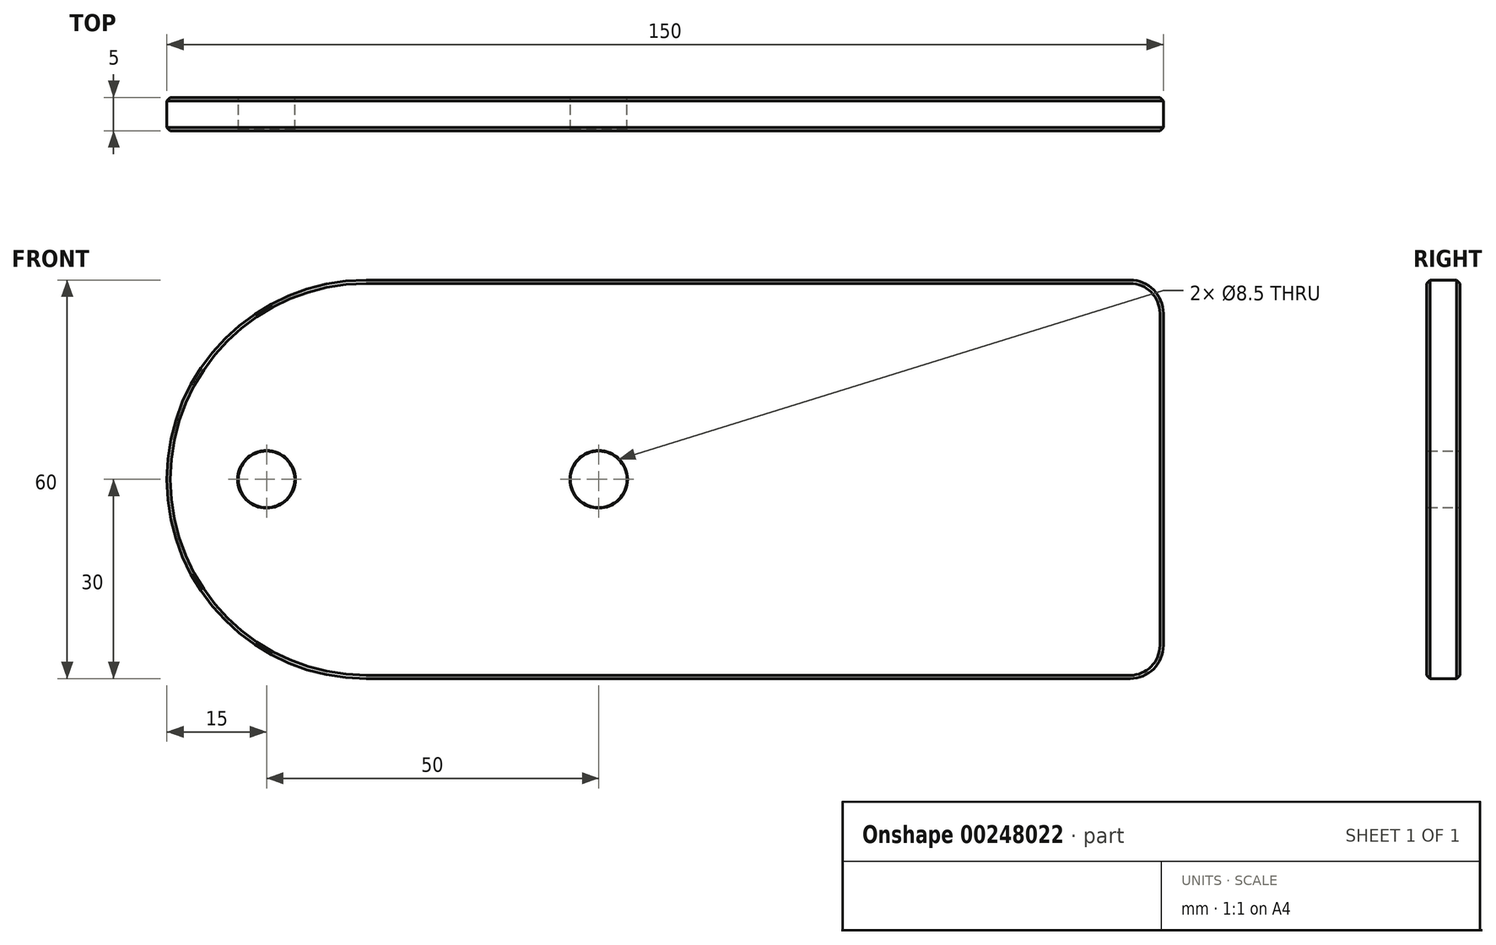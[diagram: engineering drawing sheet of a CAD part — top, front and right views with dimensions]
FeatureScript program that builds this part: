
annotation { "Feature Type Name" : "Feature", "Feature Type Description" : "" }
export const myFeature = defineFeature(function(context is Context, id is Id, definition is map)
    precondition{}
    {
        {
            var Q0;
            Q0=qCreatedBy(makeId("Front.planeOp"),FACE);
            var sketch = newSketch(context, id + "F0", { "sketchPlane" : qUnion([Q0])});
            skLineSegment(sketch, "E0.bottom", {"start": v(75, 30) * mm, "end": v(-45, 30) * mm});
            skLineSegment(sketch, "E0.top", {"start": v(75, -30) * mm, "end": v(-45, -30) * mm});
            skLineSegment(sketch, "E0.left", {"start": v(75, 30) * mm, "end": v(75, -30) * mm});
            skPoint(sketch, "E0.middle", {"position": v(0, 0) * mm});
            skPoint(sketch, "E1", {"position": v(-45, 0) * mm});
            skPoint(sketch, "E1.positionSnap0", {"position": v(-75, 0) * mm});
            skArc(sketch, "E2", {"start": v(-45, 30) * mm, "mid": v(-75, 0) * mm, "end": v(-45, -30) * mm});
            skPoint(sketch, "E3.orphan", {"position": v(-75, 30) * mm});
            skPoint(sketch, "E4.orphan", {"position": v(-75, -30) * mm});
            skPoint(sketch, "E5", {"position": v(-60, 0) * mm});
            skPoint(sketch, "E6", {"position": v(-10, 0) * mm});
            skCircle(sketch, "E7", {"center": v(-60, 0) * mm, "radius": 4.25 * mm});
            skCircle(sketch, "E8", {"center": v(-10, 0) * mm, "radius": 4.25 * mm});
            skSolve(sketch);
        }
        {
            var Q0;
            Q0=makeQuery(id+"F0.imprint","IMPRINT",FACE,{"disambiguationData":[TD([[makeQuery(id+"F0.imprint","IMPRINT",EDGE,{"derivedFrom":sQuery(id+"F0.wireOp",EDGE,"E0.bottom")}),1.0]])]});
            extrude(context, id + "F1", {"entities" : qUnion([Q0]), "depth" : 5 * mm, "offsetDistance" : 25 * mm, "symmetric" : true});
        }
        {
            var Q0;
            Q0=makeQuery(id+"F1.opExtrude","SWEPT_EDGE",EDGE,{"disambiguationData":[OSD([sQuery(id+"F0.wireOp",EDGE,"E0.top"),sQuery(id+"F0.wireOp",EDGE,"E0.left")])]});
            var Q1;
            Q1=makeQuery(id+"F1.opExtrude","SWEPT_EDGE",EDGE,{"disambiguationData":[OSD([sQuery(id+"F0.wireOp",EDGE,"E0.bottom"),sQuery(id+"F0.wireOp",EDGE,"E0.left")])]});
            fillet(context, id + "F2", {"entities" : qUnion([Q0, Q1]), "radius" : 5 * mm, "tangentPropagation" : true, "allowEdgeOverflow" : false});
        }
        {
            var Q0;
            Q0=makeQuery(id+"F1.opExtrude","CAP_EDGE",EDGE,{"disambiguationData":[OSD([sQuery(id+"F0.wireOp",EDGE,"E0.top")])],"isStart":false});
            var Q1;
            Q1=makeQuery(id+"F1.opExtrude","CAP_EDGE",EDGE,{"disambiguationData":[OSD([sQuery(id+"F0.wireOp",EDGE,"E0.bottom")])],"isStart":true});
            chamfer(context, id + "F3", {"entities" : qUnion([Q0, Q1]), "width" : 0.5 * mm, "tangentPropagation" : true});
        }
        {
            var Q0;
            Q0=makeQuery(id+"F1.opExtrude","CAP_EDGE",EDGE,{"disambiguationData":[OSD([sQuery(id+"F0.wireOp",EDGE,"E8")])],"isStart":true});
            var Q1;
            Q1=makeQuery(id+"F1.opExtrude","CAP_EDGE",EDGE,{"disambiguationData":[OSD([sQuery(id+"F0.wireOp",EDGE,"E7")])],"isStart":true});
            var Q2;
            Q2=makeQuery(id+"F1.opExtrude","CAP_EDGE",EDGE,{"disambiguationData":[OSD([sQuery(id+"F0.wireOp",EDGE,"E7")])],"isStart":false});
            var Q3;
            Q3=makeQuery(id+"F1.opExtrude","CAP_EDGE",EDGE,{"disambiguationData":[OSD([sQuery(id+"F0.wireOp",EDGE,"E8")])],"isStart":false});
            chamfer(context, id + "F4", {"entities" : qUnion([Q0, Q1, Q2, Q3]), "width" : 0.1 * mm, "tangentPropagation" : true});
        }
    });
